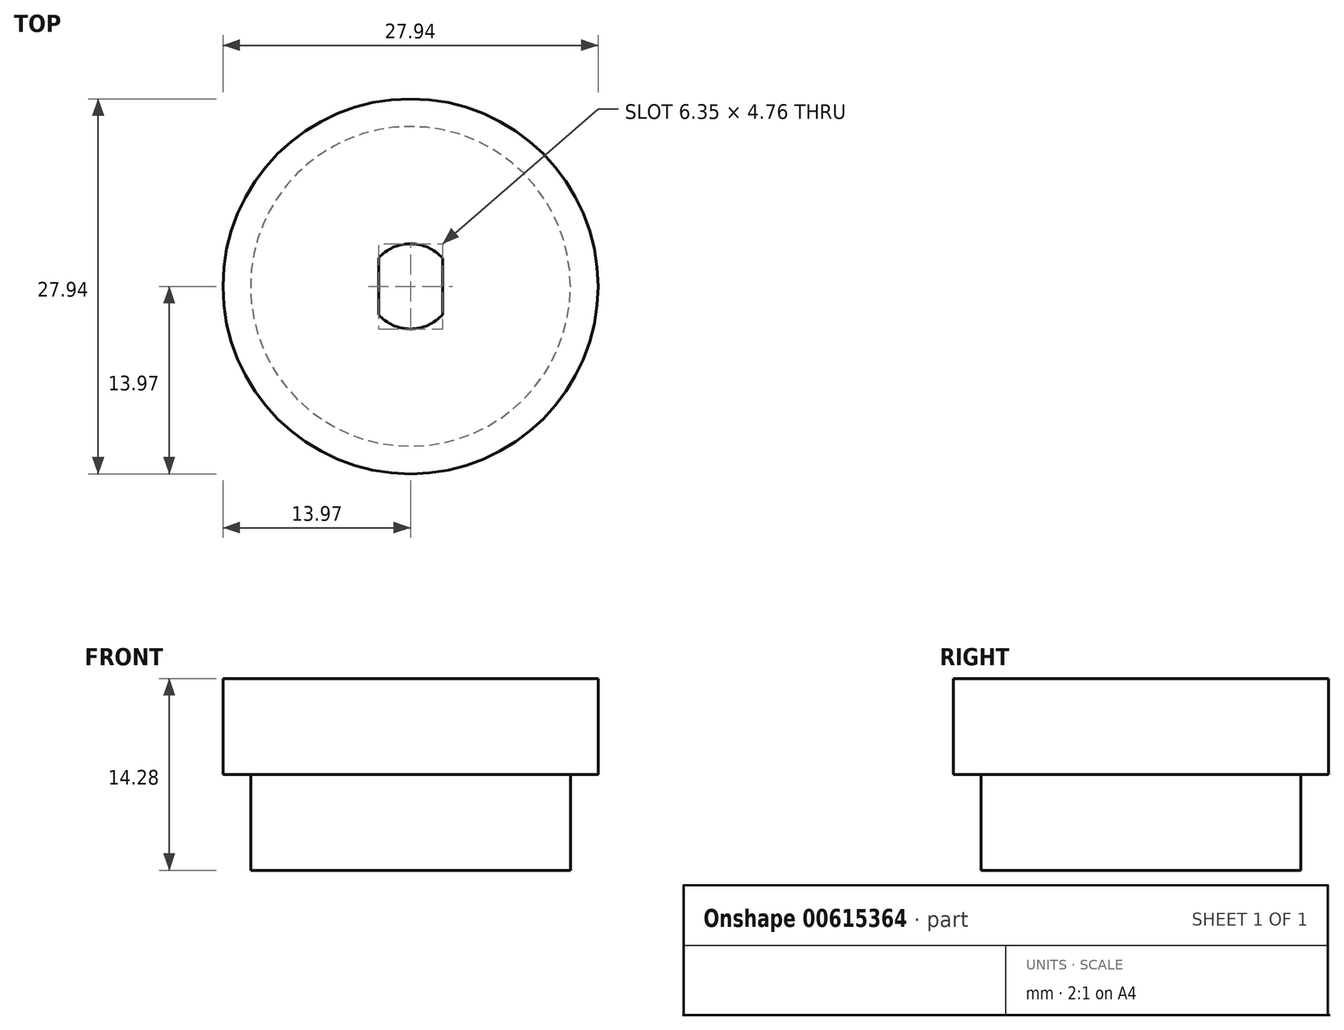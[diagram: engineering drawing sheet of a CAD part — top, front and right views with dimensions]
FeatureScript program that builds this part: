
annotation { "Feature Type Name" : "Feature", "Feature Type Description" : "" }
export const myFeature = defineFeature(function(context is Context, id is Id, definition is map)
    precondition{}
    {
        {
            var Q0;
            Q0=qCreatedBy(makeId("Top.planeOp"),FACE);
            var sketch = newSketch(context, id + "F0", { "sketchPlane" : qUnion([Q0])});
            skCircle(sketch, "E0", {"center": v(0, 0) * mm, "radius": 11.9 * mm});
            skSolve(sketch);
        }
        {
            var Q0;
            Q0=makeQuery(id+"F0.imprint","IMPRINT",FACE,{"disambiguationData":[TD([[makeQuery(id+"F0.imprint","IMPRINT",EDGE,{"derivedFrom":sQuery(id+"F0.wireOp",EDGE,"E0")}),1.0]])]});
            extrude(context, id + "F1", {"entities" : qUnion([Q0]), "oppositeDirection" : true, "depth" : 7.14 * mm, "offsetDistance" : 25.4 * mm});
        }
        {
            var Q0;
            Q0=qCreatedBy(makeId("Top.planeOp"),FACE);
            var sketch = newSketch(context, id + "F2", { "sketchPlane" : qUnion([Q0])});
            skCircle(sketch, "E1", {"center": v(0, 0) * mm, "radius": 13.97 * mm});
            skSolve(sketch);
        }
        {
            var Q0;
            Q0 = qSketchRegion(id + "F2", true);
            extrude(context, id + "F3", {"entities" : qUnion([Q0]), "operationType" : NewBodyOperationType.ADD, "depth" : 7.14 * mm, "offsetDistance" : 25.4 * mm});
        }
        {
            var Q0;
            Q0=makeQuery(id+"F3.opExtrude","CAP_FACE",FACE,{"disambiguationData":[OSD([sQuery(id+"F2.wireOp",EDGE,"E1")])],"isStart":false});
            var sketch = newSketch(context, id + "F4", { "sketchPlane" : qUnion([Q0])});
            skPoint(sketch, "E2.middle", {"position": v(0, 0) * mm});
            skArc(sketch, "E3", {"start": v(-2.1, 2.38) * mm, "mid": v(-2.25, 2.25) * mm, "end": v(-2.38, 2.1) * mm});
            skArc(sketch, "E4", {"start": v(2.38, 2.1) * mm, "mid": v(0.2, 3.17) * mm, "end": v(-2.1, 2.38) * mm});
            skLineSegment(sketch, "E5", {"start": v(2.38, 2.1) * mm, "end": v(2.38, -2.1) * mm});
            skLineSegment(sketch, "E6", {"start": v(-2.38, 2.1) * mm, "end": v(-2.38, -2.1) * mm});
            skArc(sketch, "E7", {"start": v(-2.38, -2.1) * mm, "mid": v(0, -3.18) * mm, "end": v(2.38, -2.1) * mm});
            skSolve(sketch);
        }
        {
            var Q0;
            Q0 = qSketchRegion(id + "F4", true);
            extrude(context, id + "F5", {"entities" : qUnion([Q0]), "operationType" : NewBodyOperationType.REMOVE, "oppositeDirection" : true, "depth" : 25.4 * mm, "offsetDistance" : 25.4 * mm});
        }
    });
